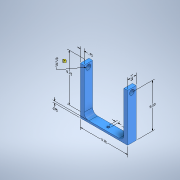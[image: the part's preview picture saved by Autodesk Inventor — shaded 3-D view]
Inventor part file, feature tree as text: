
AUTODESK INVENTOR PART (.ipt)
format: ipt  version: 2022.2 (Build 262287000, 287)  size: 303,104 bytes
history: native  units: in
note: dims shown in document units (in); Inventor stores cm internally (conversion verified against a paired STEP export)
features: other x9, sketch x5, extrude x4, thicken_offset x2, fillet x1, emboss x1
ambient origin geometry x8: Origin, YZ Plane, XZ Plane, XY Plane, X Axis, Y Axis, Z Axis, Center Point
bodies: Solid1 (feature_tree)
feature tree (22):
  other  "Annotations"
  extrude  "Extrusion1"  Depth=1.75in
  extrude  "Extrusion2"  Depth=0.375in
  extrude  "Extrusion3"  Depth=9.375in TaperAngle=0.0deg
  extrude  "Extrusion4"  TaperAngle=0.0deg  [1 undecoded]
  thicken_offset  "Thicken1"
  thicken_offset  "Thicken2"
  fillet  "Fillet2"  Radius=0.5in
  emboss  "Emboss1"
  sketch  "Sketch1"  dims[d0=9.7in d1=1.75in]
  sketch  "Sketch2"  dims[d2=0.375in d3=0.0in d4=0.75in]
  sketch  "Sketch3"  dims[d5=0.75in d6=9.375in d7=0.0in]
  sketch  "Sketch4"  dims[d8=1.0in d10=0.0in d11=0.0in d13=0.5in]
  sketch  "Sketch5"  dims[d14=0.0in d15=0.0in d16=0.005in d17=0.005in d18=0.005in d19=0.005in d22=1.0in d28=0.75in d39=0.1in d40=0.0in d23=0.1417in d24=0.375in d25=0.2606in d26=0.1203in d27=9.75in d30=0.2925in d31=0.3111in d32=0.75in d33=0.2465in d34=0.1211in d35=1.75in d36=0.0895in d37=0.24in d38=9.7in d41=0.1295in d42=9.0in d43=0.1802in d44=1.01in d45=0.1904in d46=0.1841in d47=0.5in]
  other  "Linear Dimension 1"
  other  "Linear Dimension 2"
  other  "Linear Dimension 3"
  other  "Linear Dimension 4"
  other  "Linear Dimension 5"
  other  "Linear Dimension 6"
  other  "Diameter Dimension 1"
  other  "Linear Dimension 7"
note: 1 required parameter value undecoded (feature->parameter linkage not recoverable at this tier; creation-order binding heuristic only, values carry confidence <= 0.55)
